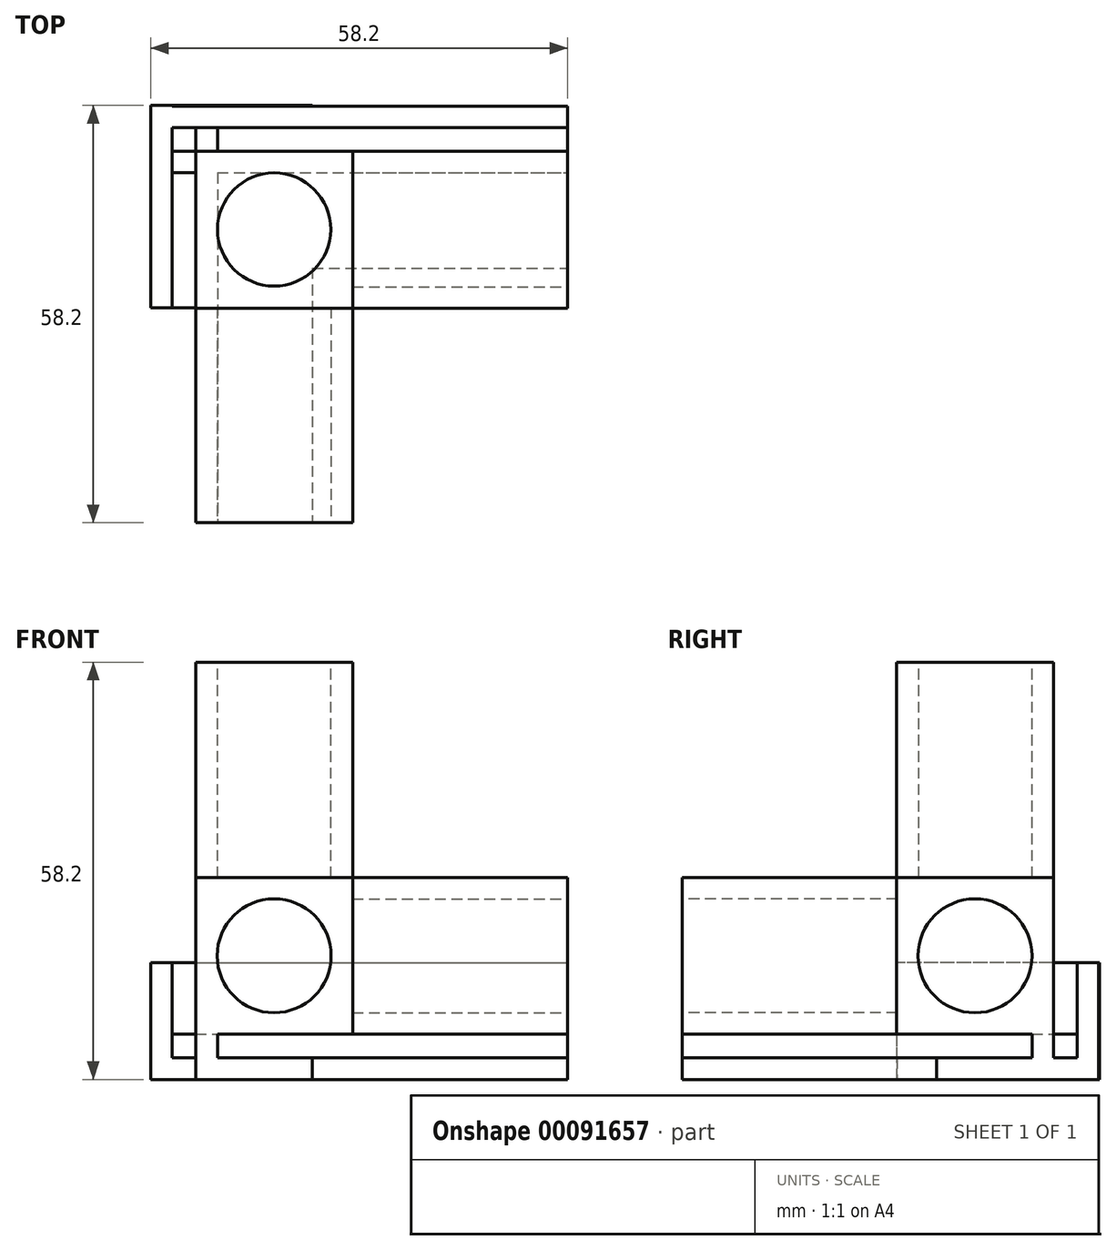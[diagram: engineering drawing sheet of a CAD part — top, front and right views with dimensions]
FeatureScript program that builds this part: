
annotation { "Feature Type Name" : "Feature", "Feature Type Description" : "" }
export const myFeature = defineFeature(function(context is Context, id is Id, definition is map)
    precondition{}
    {
        {
            var Q0;
            Q0=qCreatedBy(makeId("Front.planeOp"),FACE);
            var sketch = newSketch(context, id + "F0", { "sketchPlane" : qUnion([Q0])});
            skLineSegment(sketch, "E0.bottom", {"start": v(-42.3, 45.9) * mm, "end": v(-26.4, 45.9) * mm});
            skLineSegment(sketch, "E0.top", {"start": v(-42.3, 0) * mm, "end": v(-26.4, 0) * mm});
            skLineSegment(sketch, "E0.left", {"start": v(-42.3, 45.9) * mm, "end": v(-42.3, 0) * mm});
            skLineSegment(sketch, "E0.right", {"start": v(-26.4, 45.9) * mm, "end": v(-26.4, 15.9) * mm});
            skLineSegment(sketch, "E1.top", {"start": v(-42.3, 15.9) * mm, "end": v(-26.4, 15.9) * mm});
            skLineSegment(sketch, "E1.left", {"start": v(-42.3, 0) * mm, "end": v(-42.3, 15.9) * mm});
            skLineSegment(sketch, "E1.right", {"start": v(3.6, 0) * mm, "end": v(3.6, 15.9) * mm});
            skLineSegment(sketch, "E2", {"start": v(-26.4, 15.9) * mm, "end": v(-26.4, 0) * mm});
            skLineSegment(sketch, "E3", {"start": v(-26.4, 15.9) * mm, "end": v(3.6, 15.9) * mm});
            skLineSegment(sketch, "E4", {"start": v(-26.4, 0) * mm, "end": v(-26.4, 0) * mm});
            skLineSegment(sketch, "E5", {"start": v(-42.3, 15.9) * mm, "end": v(-42.3, 15.9) * mm});
            skLineSegment(sketch, "E6", {"start": v(-26.4, 0) * mm, "end": v(3.6, 0) * mm});
            skLineSegment(sketch, "E7.0", {"start": v(-45.3, 48.9) * mm, "end": v(-45.3, -3) * mm});
            skLineSegment(sketch, "E7.1", {"start": v(-45.3, -3) * mm, "end": v(-23.4, -3) * mm});
            skLineSegment(sketch, "E7.2", {"start": v(-23.4, 48.9) * mm, "end": v(-23.4, 18.9) * mm});
            skLineSegment(sketch, "E7.3", {"start": v(-23.4, 18.9) * mm, "end": v(6.6, 18.9) * mm});
            skLineSegment(sketch, "E7.4", {"start": v(6.6, -3) * mm, "end": v(6.6, 18.9) * mm});
            skLineSegment(sketch, "E7.5", {"start": v(-45.3, 48.9) * mm, "end": v(-23.4, 48.9) * mm});
            skLineSegment(sketch, "E7.6", {"start": v(-23.4, -3) * mm, "end": v(6.6, -3) * mm});
            skPoint(sketch, "E8", {"position": v(-34.36, 7.95) * mm});
            skPoint(sketch, "E8.positionSnap0", {"position": v(-26.4, 7.95) * mm});
            skPoint(sketch, "E8.positionSnap1", {"position": v(-34.36, 15.9) * mm});
            skCircle(sketch, "E9", {"center": v(-34.36, 7.95) * mm, "radius": 7.95 * mm});
            skLineSegment(sketch, "E10", {"start": v(-23.4, 18.9) * mm, "end": v(-45.3, 18.9) * mm});
            skLineSegment(sketch, "E11", {"start": v(-23.4, 18.9) * mm, "end": v(-23.4, -3) * mm});
            skSolve(sketch);
        }
        {
            var Q0;
            {var subQ1=sQuery(id+"F0.wireOp",EDGE,"E1.top");var subQ3=sQuery(id+"F0.wireOp",EDGE,"E9");var subQ4=makeQuery(id+"F0.imprint","INTERSECT",VERTEX,{"derivedFrom":[subQ1,subQ3]});Q0=makeQuery(id+"F0.imprint","IMPRINT",FACE,{"disambiguationData":[TD([[makeQuery(id+"F0.imprint","IMPRINT",EDGE,{"disambiguationData":[TD([[subQ4,-1.0]])],"derivedFrom":subQ3}),-1.0]])]});}
            var Q1;
            {var subQ0=sQuery(id+"F0.wireOp",EDGE,"E9");var subQ1=makeQuery(id+"F0.imprint","INTERSECT",VERTEX,{"derivedFrom":[sQuery(id+"F0.wireOp",EDGE,"E1.top"),subQ0]});Q1=makeQuery(id+"F0.imprint","IMPRINT",FACE,{"disambiguationData":[TD([[makeQuery(id+"F0.imprint","IMPRINT",EDGE,{"disambiguationData":[TD([[subQ1,1.0]])],"derivedFrom":subQ0}),1.0]])]});}
            var Q2;
            {var subQ5=sQuery(id+"F0.wireOp",EDGE,"E0.bottom");Q2=makeQuery(id+"F0.imprint","IMPRINT",FACE,{"disambiguationData":[TD([[makeQuery(id+"F0.imprint","IMPRINT",EDGE,{"derivedFrom":subQ5}),1.0]])]});}
            var Q3;
            {var subQ0=sQuery(id+"F0.wireOp",EDGE,"E1.right");Q3=makeQuery(id+"F0.imprint","IMPRINT",FACE,{"disambiguationData":[TD([[makeQuery(id+"F0.imprint","IMPRINT",EDGE,{"derivedFrom":subQ0}),1.0]])]});}
            var Q4;
            {var subQ0=sQuery(id+"F0.wireOp",EDGE,"E0.bottom");Q4=makeQuery(id+"F0.imprint","IMPRINT",FACE,{"disambiguationData":[TD([[makeQuery(id+"F0.imprint","IMPRINT",EDGE,{"derivedFrom":subQ0}),-1.0]])]});}
            var Q5;
            {var subQ0=sQuery(id+"F0.wireOp",EDGE,"E1.left");var subQ1=sQuery(id+"F0.wireOp",EDGE,"E0.top");var subQ2=makeQuery(id+"F0.imprint","INTERSECT",VERTEX,{"derivedFrom":[subQ1,subQ0]});Q5=makeQuery(id+"F0.imprint","IMPRINT",FACE,{"disambiguationData":[TD([[makeQuery(id+"F0.imprint","IMPRINT",EDGE,{"disambiguationData":[TD([[subQ2,-1.0]])],"derivedFrom":subQ1}),1.0]])]});}
            var Q6;
            {var subQ1=sQuery(id+"F0.wireOp",EDGE,"E0.top");var subQ3=sQuery(id+"F0.wireOp",EDGE,"E9");var subQ4=makeQuery(id+"F0.imprint","INTERSECT",VERTEX,{"derivedFrom":[subQ1,subQ3]});Q6=makeQuery(id+"F0.imprint","IMPRINT",FACE,{"disambiguationData":[TD([[makeQuery(id+"F0.imprint","IMPRINT",EDGE,{"disambiguationData":[TD([[subQ4,-1.0]])],"derivedFrom":subQ3}),-1.0]])]});}
            var Q7;
            {var subQ1=sQuery(id+"F0.wireOp",EDGE,"E1.top");var subQ3=sQuery(id+"F0.wireOp",EDGE,"E9");var subQ4=makeQuery(id+"F0.imprint","INTERSECT",VERTEX,{"derivedFrom":[subQ1,subQ3]});Q7=makeQuery(id+"F0.imprint","IMPRINT",FACE,{"disambiguationData":[TD([[makeQuery(id+"F0.imprint","IMPRINT",EDGE,{"disambiguationData":[TD([[subQ4,1.0]])],"derivedFrom":subQ3}),-1.0]])]});}
            var Q8;
            {var subQ5=sQuery(id+"F0.wireOp",EDGE,"E1.right");Q8=makeQuery(id+"F0.imprint","IMPRINT",FACE,{"disambiguationData":[TD([[makeQuery(id+"F0.imprint","IMPRINT",EDGE,{"derivedFrom":subQ5}),-1.0]])]});}
            var Q9;
            {var subQ4=sQuery(id+"F0.wireOp",EDGE,"E0.left");var subQ6=sQuery(id+"F0.wireOp",EDGE,"E10");var subQ8=makeQuery(id+"F0.imprint","INTERSECT",VERTEX,{"derivedFrom":[subQ4,subQ6]});Q9=makeQuery(id+"F0.imprint","IMPRINT",FACE,{"disambiguationData":[TD([[makeQuery(id+"F0.imprint","IMPRINT",EDGE,{"disambiguationData":[TD([[subQ8,1.0]])],"derivedFrom":subQ6}),1.0]])]});}
            var Q10;
            {var subQ3=sQuery(id+"F0.wireOp",EDGE,"E11");var subQ5=sQuery(id+"F0.wireOp",EDGE,"E3");var subQ8=makeQuery(id+"F0.imprint","INTERSECT",VERTEX,{"derivedFrom":[subQ5,subQ3]});Q10=makeQuery(id+"F0.imprint","IMPRINT",FACE,{"disambiguationData":[TD([[makeQuery(id+"F0.imprint","IMPRINT",EDGE,{"disambiguationData":[TD([[subQ8,-1.0]])],"derivedFrom":subQ3}),-1.0]])]});}
            var Q11;
            {var subQ14=sQuery(id+"F0.wireOp",EDGE,"E7.1");Q11=makeQuery(id+"F0.imprint","IMPRINT",FACE,{"disambiguationData":[TD([[makeQuery(id+"F0.imprint","IMPRINT",EDGE,{"derivedFrom":subQ14}),1.0]])]});}
            var Q12;
            {var subQ1=sQuery(id+"F0.wireOp",EDGE,"E0.right");var subQ3=sQuery(id+"F0.wireOp",EDGE,"E10");var subQ4=makeQuery(id+"F0.imprint","INTERSECT",VERTEX,{"derivedFrom":[subQ1,subQ3]});Q12=makeQuery(id+"F0.imprint","IMPRINT",FACE,{"disambiguationData":[TD([[makeQuery(id+"F0.imprint","IMPRINT",EDGE,{"disambiguationData":[TD([[subQ4,-1.0]])],"derivedFrom":subQ1}),1.0]])]});}
            extrude(context, id + "F1", {"entities" : qUnion([Q0, Q1, Q2, Q3, Q4, Q5, Q6, Q7, Q8, Q9, Q10, Q11, Q12]), "depth" : (15.9 + 6) * mm});
        }
        {
            var Q0;
            {var subQ14=sQuery(id+"F0.wireOp",EDGE,"E7.1");Q0=makeQuery(id+"F0.imprint","IMPRINT",FACE,{"disambiguationData":[TD([[makeQuery(id+"F0.imprint","IMPRINT",EDGE,{"derivedFrom":subQ14}),1.0]])]});}
            var Q1;
            {var subQ0=sQuery(id+"F0.wireOp",EDGE,"E9");var subQ1=makeQuery(id+"F0.imprint","INTERSECT",VERTEX,{"derivedFrom":[sQuery(id+"F0.wireOp",EDGE,"E1.top"),subQ0]});Q1=makeQuery(id+"F0.imprint","IMPRINT",FACE,{"disambiguationData":[TD([[makeQuery(id+"F0.imprint","IMPRINT",EDGE,{"disambiguationData":[TD([[subQ1,1.0]])],"derivedFrom":subQ0}),1.0]])]});}
            var Q2;
            {var subQ4=sQuery(id+"F0.wireOp",EDGE,"E0.left");var subQ6=sQuery(id+"F0.wireOp",EDGE,"E10");var subQ8=makeQuery(id+"F0.imprint","INTERSECT",VERTEX,{"derivedFrom":[subQ4,subQ6]});Q2=makeQuery(id+"F0.imprint","IMPRINT",FACE,{"disambiguationData":[TD([[makeQuery(id+"F0.imprint","IMPRINT",EDGE,{"disambiguationData":[TD([[subQ8,1.0]])],"derivedFrom":subQ6}),1.0]])]});}
            var Q3;
            {var subQ3=sQuery(id+"F0.wireOp",EDGE,"E11");var subQ5=sQuery(id+"F0.wireOp",EDGE,"E3");var subQ8=makeQuery(id+"F0.imprint","INTERSECT",VERTEX,{"derivedFrom":[subQ5,subQ3]});Q3=makeQuery(id+"F0.imprint","IMPRINT",FACE,{"disambiguationData":[TD([[makeQuery(id+"F0.imprint","IMPRINT",EDGE,{"disambiguationData":[TD([[subQ8,-1.0]])],"derivedFrom":subQ3}),-1.0]])]});}
            var Q4;
            {var subQ1=sQuery(id+"F0.wireOp",EDGE,"E0.right");var subQ3=sQuery(id+"F0.wireOp",EDGE,"E10");var subQ4=makeQuery(id+"F0.imprint","INTERSECT",VERTEX,{"derivedFrom":[subQ1,subQ3]});Q4=makeQuery(id+"F0.imprint","IMPRINT",FACE,{"disambiguationData":[TD([[makeQuery(id+"F0.imprint","IMPRINT",EDGE,{"disambiguationData":[TD([[subQ4,-1.0]])],"derivedFrom":subQ1}),1.0]])]});}
            var Q5;
            {var subQ1=sQuery(id+"F0.wireOp",EDGE,"E1.top");var subQ3=sQuery(id+"F0.wireOp",EDGE,"E9");var subQ4=makeQuery(id+"F0.imprint","INTERSECT",VERTEX,{"derivedFrom":[subQ1,subQ3]});Q5=makeQuery(id+"F0.imprint","IMPRINT",FACE,{"disambiguationData":[TD([[makeQuery(id+"F0.imprint","IMPRINT",EDGE,{"disambiguationData":[TD([[subQ4,1.0]])],"derivedFrom":subQ3}),-1.0]])]});}
            var Q6;
            {var subQ1=sQuery(id+"F0.wireOp",EDGE,"E1.top");var subQ3=sQuery(id+"F0.wireOp",EDGE,"E9");var subQ4=makeQuery(id+"F0.imprint","INTERSECT",VERTEX,{"derivedFrom":[subQ1,subQ3]});Q6=makeQuery(id+"F0.imprint","IMPRINT",FACE,{"disambiguationData":[TD([[makeQuery(id+"F0.imprint","IMPRINT",EDGE,{"disambiguationData":[TD([[subQ4,-1.0]])],"derivedFrom":subQ3}),-1.0]])]});}
            var Q7;
            {var subQ0=sQuery(id+"F0.wireOp",EDGE,"E1.left");var subQ1=sQuery(id+"F0.wireOp",EDGE,"E0.top");var subQ2=makeQuery(id+"F0.imprint","INTERSECT",VERTEX,{"derivedFrom":[subQ1,subQ0]});Q7=makeQuery(id+"F0.imprint","IMPRINT",FACE,{"disambiguationData":[TD([[makeQuery(id+"F0.imprint","IMPRINT",EDGE,{"disambiguationData":[TD([[subQ2,-1.0]])],"derivedFrom":subQ1}),1.0]])]});}
            var Q8;
            {var subQ1=sQuery(id+"F0.wireOp",EDGE,"E0.top");var subQ3=sQuery(id+"F0.wireOp",EDGE,"E9");var subQ4=makeQuery(id+"F0.imprint","INTERSECT",VERTEX,{"derivedFrom":[subQ1,subQ3]});Q8=makeQuery(id+"F0.imprint","IMPRINT",FACE,{"disambiguationData":[TD([[makeQuery(id+"F0.imprint","IMPRINT",EDGE,{"disambiguationData":[TD([[subQ4,-1.0]])],"derivedFrom":subQ3}),-1.0]])]});}
            extrude(context, id + "F2", {"entities" : qUnion([Q0, Q1, Q2, Q3, Q4, Q5, Q6, Q7, Q8]), "operationType" : NewBodyOperationType.ADD, "depth" : (15.8 + 6 + 30) * mm});
        }
        {
            var Q0;
            Q0=makeQuery(id+"F2.opExtrude","CAP_FACE",FACE,{"disambiguationData":[OSD([sQuery(id+"F0.wireOp",EDGE,"E7.0"),sQuery(id+"F0.wireOp",EDGE,"E7.1"),sQuery(id+"F0.wireOp",EDGE,"E10"),sQuery(id+"F0.wireOp",EDGE,"E11")])],"isStart":false});
            var sketch = newSketch(context, id + "F3", { "sketchPlane" : qUnion([Q0])});
            skCircle(sketch, "E12.0", {"center": v(-34.36, 7.95) * mm, "radius": 7.95 * mm});
            skSolve(sketch);
        }
        {
            var Q0;
            Q0=makeQuery(id+"F1.opExtrude","SWEPT_FACE",FACE,{"disambiguationData":[OSD([sQuery(id+"F0.wireOp",EDGE,"E7.5")])]});
            var sketch = newSketch(context, id + "F4", { "sketchPlane" : qUnion([Q0])});
            skPoint(sketch, "E13", {"position": v(-34.36, -3) * mm});
            skPoint(sketch, "E14", {"position": v(-26.4, -10.9) * mm});
            skPoint(sketch, "E15", {"position": v(-34.36, -10.9) * mm});
            skPoint(sketch, "E16", {"position": v(-62.98, 75) * mm});
            skPoint(sketch, "E17.orphan", {"position": v(-42.3, -3) * mm});
            skPoint(sketch, "E18.orphan", {"position": v(-26.4, -3) * mm});
            skPoint(sketch, "E19.orphan", {"position": v(-26.4, -18.8) * mm});
            skCircle(sketch, "E20", {"center": v(-34.36, -10.9) * mm, "radius": 7.9 * mm});
            skSolve(sketch);
        }
        {
            var Q0;
            Q0=makeQuery(id+"F1.opExtrude","SWEPT_FACE",FACE,{"disambiguationData":[OSD([sQuery(id+"F0.wireOp",EDGE,"E7.4")])]});
            var sketch = newSketch(context, id + "F5", { "sketchPlane" : qUnion([Q0])});
            skLineSegment(sketch, "E21.0", {"start": v(-18.9, 15.9) * mm, "end": v(-3, 15.9) * mm});
            skLineSegment(sketch, "E21.1", {"start": v(-18.9, 0) * mm, "end": v(-18.9, 15.9) * mm});
            skLineSegment(sketch, "E21.2", {"start": v(-18.9, 0) * mm, "end": v(-3, 0) * mm});
            skLineSegment(sketch, "E21.3", {"start": v(-3, 0) * mm, "end": v(-3, 15.9) * mm});
            skCircle(sketch, "E22", {"center": v(-10.95, 7.95) * mm, "radius": 7.95 * mm});
            skPoint(sketch, "E22.centerSnap0", {"position": v(-10.95, 0) * mm});
            skPoint(sketch, "E22.centerSnap1", {"position": v(-3, 7.95) * mm});
            skSolve(sketch);
        }
        {
            var Q0;
            Q0=makeQuery(id+"F3.imprint","IMPRINT",FACE,{"disambiguationData":[TD([[makeQuery(id+"F3.imprint","IMPRINT",EDGE,{"derivedFrom":sQuery(id+"F3.wireOp",EDGE,"E12.0")}),1.0]])]});
            extrude(context, id + "F6", {"entities" : qUnion([Q0]), "operationType" : NewBodyOperationType.REMOVE, "oppositeDirection" : true, "depth" : 30 * mm});
        }
        {
            var Q0;
            {var subQ0=sQuery(id+"F5.wireOp",EDGE,"E22");var subQ1=makeQuery(id+"F5.imprint","INTERSECT",VERTEX,{"derivedFrom":[sQuery(id+"F5.wireOp",EDGE,"E21.1"),subQ0]});Q0=makeQuery(id+"F5.imprint","IMPRINT",FACE,{"disambiguationData":[TD([[makeQuery(id+"F5.imprint","IMPRINT",EDGE,{"disambiguationData":[TD([[subQ1,1.0]])],"derivedFrom":subQ0}),1.0]])]});}
            extrude(context, id + "F7", {"entities" : qUnion([Q0]), "operationType" : NewBodyOperationType.REMOVE, "oppositeDirection" : true, "depth" : 30 * mm});
        }
        {
            var Q0;
            Q0=makeQuery(id+"F4.imprint","IMPRINT",FACE,{"disambiguationData":[TD([[makeQuery(id+"F4.imprint","IMPRINT",EDGE,{"derivedFrom":sQuery(id+"F4.wireOp",EDGE,"E20")}),1.0]])]});
            var Q1;
            Q1=sQuery(id+"F4.wireOp",EDGE,"E20");
            extrude(context, id + "F8", {"entities" : qUnion([Q0]), "operationType" : NewBodyOperationType.REMOVE, "surfaceEntities" : qUnion([Q1]), "oppositeDirection" : true, "depth" : 30 * mm});
        }
        {
            assignVariable(context, id + "F9", {"name" : "extrude", "anyValue" : 6 + 15.9 + 30});
        }
        {
            var Q0;
            Q0=makeQuery(id+"F2.opExtrude","CAP_FACE",FACE,{"disambiguationData":[OSD([sQuery(id+"F0.wireOp",EDGE,"E7.0"),sQuery(id+"F0.wireOp",EDGE,"E7.1"),sQuery(id+"F0.wireOp",EDGE,"E10"),sQuery(id+"F0.wireOp",EDGE,"E11")])],"isStart":false});
            var sketch = newSketch(context, id + "F10", { "sketchPlane" : qUnion([Q0])});
            skLineSegment(sketch, "E23", {"start": v(-45.3, -3) * mm, "end": v(-45.3, -9.3) * mm});
            skLineSegment(sketch, "E24", {"start": v(-45.3, -9.3) * mm, "end": v(-29, -9.3) * mm});
            skLineSegment(sketch, "E25", {"start": v(-29, -9.3) * mm, "end": v(-29, -6.3) * mm});
            skLineSegment(sketch, "E26", {"start": v(-29, -6.3) * mm, "end": v(-42.26, -6.3) * mm});
            skLineSegment(sketch, "E27", {"start": v(-42.26, -6.3) * mm, "end": v(-42.26, -3) * mm});
            skLineSegment(sketch, "E28", {"start": v(-45.3, -9.3) * mm, "end": v(-51.6, -9.3) * mm});
            skLineSegment(sketch, "E29", {"start": v(-51.6, -9.3) * mm, "end": v(-51.6, 7) * mm});
            skLineSegment(sketch, "E30", {"start": v(-51.6, 7) * mm, "end": v(-48.6, 7) * mm});
            skLineSegment(sketch, "E31", {"start": v(-45.3, -6.3) * mm, "end": v(-48.6, -6.3) * mm});
            skLineSegment(sketch, "E32", {"start": v(-48.6, -6.3) * mm, "end": v(-48.6, 7) * mm});
            skSolve(sketch);
        }
        {
            var Q0;
            Q0=makeQuery(id+"F1.opExtrude","SWEPT_FACE",FACE,{"disambiguationData":[OSD([sQuery(id+"F0.wireOp",EDGE,"E7.4")])]});
            var sketch = newSketch(context, id + "F11", { "sketchPlane" : qUnion([Q0])});
            skLineSegment(sketch, "E33", {"start": v(0, -3) * mm, "end": v(0, -9.3) * mm});
            skLineSegment(sketch, "E34", {"start": v(0, -9.3) * mm, "end": v(-16.3, -9.3) * mm});
            skLineSegment(sketch, "E35", {"start": v(-16.3, -9.3) * mm, "end": v(-16.3, -6.3) * mm});
            skLineSegment(sketch, "E36", {"start": v(-16.3, -6.3) * mm, "end": v(-3, -6.3) * mm});
            skLineSegment(sketch, "E37", {"start": v(-3, -6.3) * mm, "end": v(-3, -3) * mm});
            skLineSegment(sketch, "E38", {"start": v(0, -9.3) * mm, "end": v(6.3, -9.3) * mm});
            skLineSegment(sketch, "E39", {"start": v(6.3, -9.3) * mm, "end": v(6.3, 7) * mm});
            skLineSegment(sketch, "E40", {"start": v(6.3, 7) * mm, "end": v(3.3, 7) * mm});
            skLineSegment(sketch, "E41", {"start": v(3.3, 7) * mm, "end": v(3.3, -6.3) * mm});
            skLineSegment(sketch, "E42", {"start": v(3.3, -6.3) * mm, "end": v(0, -6.3) * mm});
            skSolve(sketch);
        }
        {
            var Q0;
            {var subQ0=sQuery(id+"F10.wireOp",EDGE,"E28");Q0=makeQuery(id+"F10.imprint","IMPRINT",FACE,{"disambiguationData":[TD([[makeQuery(id+"F10.imprint","IMPRINT",EDGE,{"derivedFrom":subQ0}),-1.0]])]});}
            var Q1;
            {var subQ0=sQuery(id+"F10.wireOp",EDGE,"E24");Q1=makeQuery(id+"F10.imprint","IMPRINT",FACE,{"disambiguationData":[TD([[makeQuery(id+"F10.imprint","IMPRINT",EDGE,{"derivedFrom":subQ0}),1.0]])]});}
            extrude(context, id + "F12", {"entities" : qUnion([Q0, Q1]), "operationType" : NewBodyOperationType.ADD, "oppositeDirection" : true, "depth" : (getVariable(context, 'extrude') + 6.3) * mm});
        }
        {
            var Q0;
            {var subQ0=sQuery(id+"F11.wireOp",EDGE,"E34");Q0=makeQuery(id+"F11.imprint","IMPRINT",FACE,{"disambiguationData":[TD([[makeQuery(id+"F11.imprint","IMPRINT",EDGE,{"derivedFrom":subQ0}),-1.0]])]});}
            var Q1;
            {var subQ0=sQuery(id+"F11.wireOp",EDGE,"E38");Q1=makeQuery(id+"F11.imprint","IMPRINT",FACE,{"disambiguationData":[TD([[makeQuery(id+"F11.imprint","IMPRINT",EDGE,{"derivedFrom":subQ0}),1.0]])]});}
            var Q2;
            Q2=makeQuery(id+"F12.opExtrude","SWEPT_FACE",FACE,{"disambiguationData":[OSD([sQuery(id+"F10.wireOp",EDGE,"E29")])]});
            extrude(context, id + "F13", {"entities" : qUnion([Q0, Q1]), "operationType" : NewBodyOperationType.ADD, "endBound" : BoundingType.UP_TO_SURFACE, "oppositeDirection" : true, "endBoundEntityFace" : qUnion([Q2]), "depth" : 25 * mm});
        }
        {
            var Q0;
            {var subQ0=sQuery(id+"F10.wireOp",EDGE,"E28");Q0=makeQuery(id+"F10.imprint","IMPRINT",FACE,{"disambiguationData":[TD([[makeQuery(id+"F10.imprint","IMPRINT",EDGE,{"derivedFrom":subQ0}),-1.0]])]});}
            extrude(context, id + "F14", {"entities" : qUnion([Q0]), "operationType" : NewBodyOperationType.REMOVE, "oppositeDirection" : true, "depth" : 30 * mm});
        }
    });
